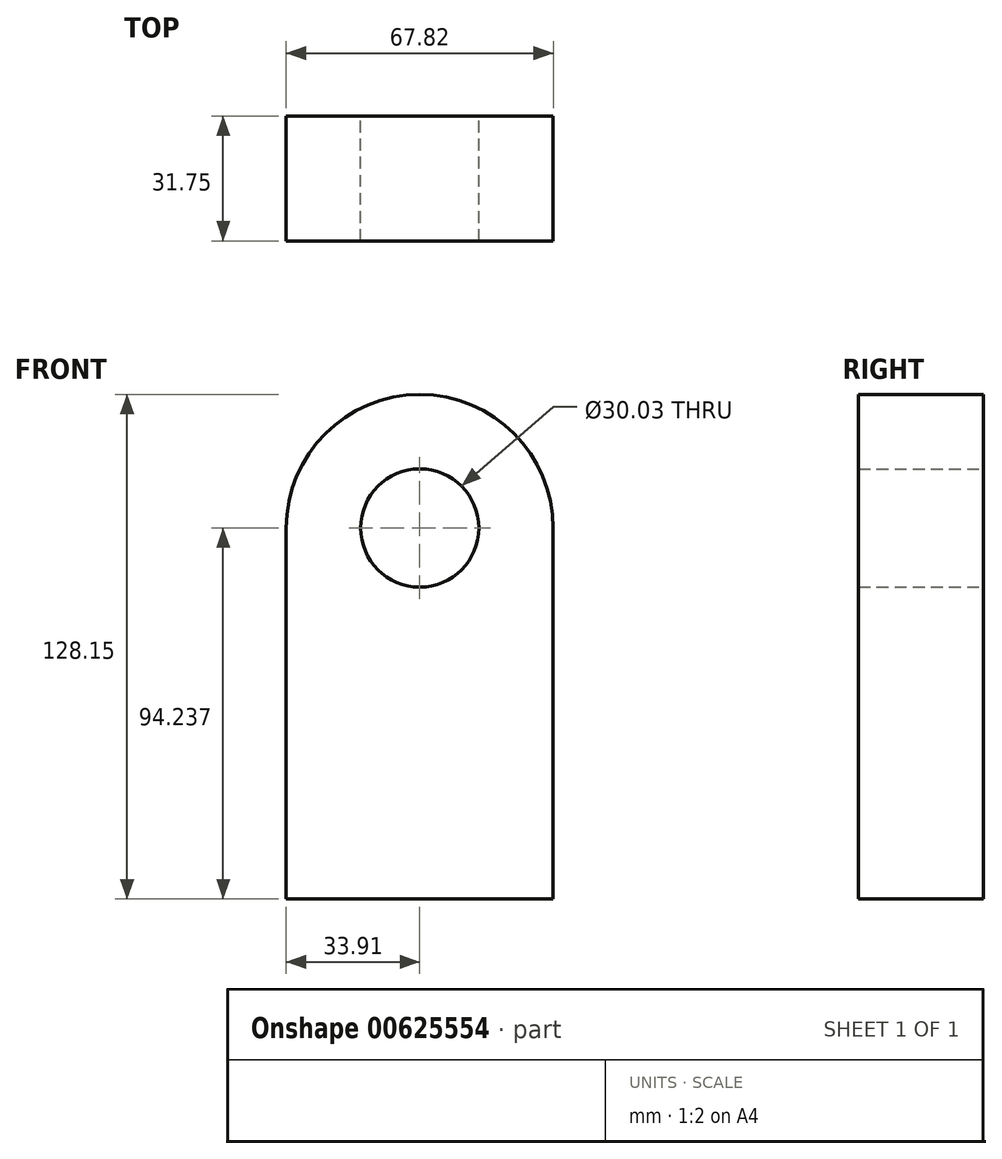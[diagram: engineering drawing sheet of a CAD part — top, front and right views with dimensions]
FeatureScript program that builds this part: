
annotation { "Feature Type Name" : "Feature", "Feature Type Description" : "" }
export const myFeature = defineFeature(function(context is Context, id is Id, definition is map)
    precondition{}
    {
        {
            var Q0;
            Q0=qCreatedBy(makeId("Front.planeOp"),FACE);
            var sketch = newSketch(context, id + "F0", { "sketchPlane" : qUnion([Q0])});
            skLineSegment(sketch, "E0.bottom", {"start": v(-33.9, 47.12) * mm, "end": v(33.9, 47.12) * mm});
            skLineSegment(sketch, "E0.top", {"start": v(-33.9, -47.12) * mm, "end": v(33.9, -47.12) * mm});
            skLineSegment(sketch, "E0.left", {"start": v(-33.9, 47.12) * mm, "end": v(-33.9, -47.12) * mm});
            skLineSegment(sketch, "E0.right", {"start": v(33.9, 47.12) * mm, "end": v(33.9, -47.12) * mm});
            skPoint(sketch, "E0.middle", {"position": v(0, 0) * mm});
            skArc(sketch, "E1", {"start": v(33.9, 47.12) * mm, "mid": v(0, 81.03) * mm, "end": v(-33.9, 47.12) * mm});
            skCircle(sketch, "E2", {"center": v(0, 47.12) * mm, "radius": 15.02 * mm});
            skSolve(sketch);
        }
        {
            var Q0;
            Q0 = qSketchRegion(id + "F0", true);
            extrude(context, id + "F1", {"entities" : qUnion([Q0]), "depth" : 31.75 * mm, "offsetDistance" : 25.4 * mm});
        }
    });
